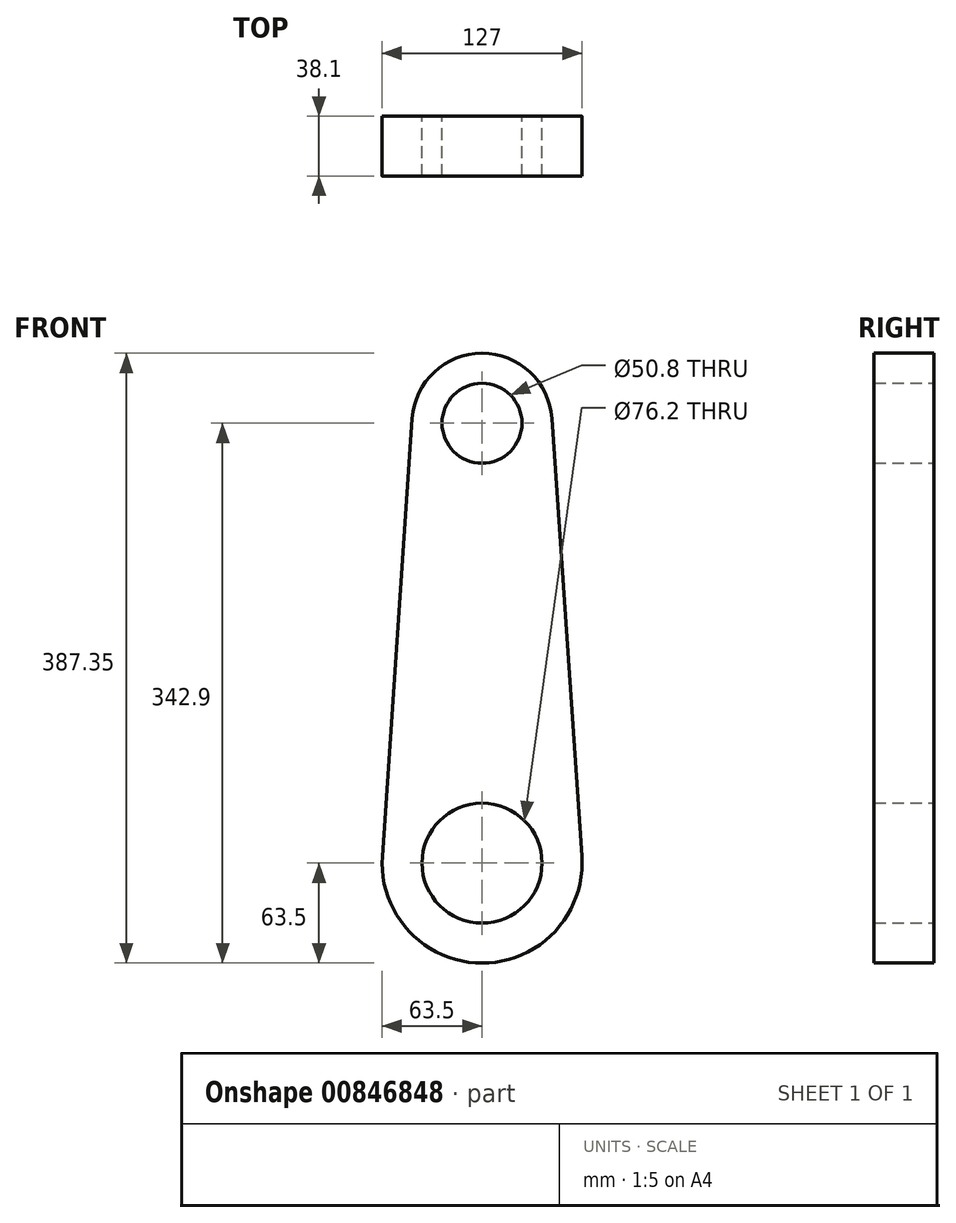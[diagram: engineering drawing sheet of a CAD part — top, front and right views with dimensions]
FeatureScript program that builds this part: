
annotation { "Feature Type Name" : "Feature", "Feature Type Description" : "" }
export const myFeature = defineFeature(function(context is Context, id is Id, definition is map)
    precondition{}
    {
        {
            var Q0;
            Q0=qCreatedBy(makeId("Front.planeOp"),FACE);
            var sketch = newSketch(context, id + "F0", { "sketchPlane" : qUnion([Q0])});
            skArc(sketch, "E0", {"start": v(-63.35, 4.33) * mm, "mid": v(0, -63.5) * mm, "end": v(63.35, 4.33) * mm});
            skArc(sketch, "E1", {"start": v(44.35, 282.43) * mm, "mid": v(0, 323.85) * mm, "end": v(-44.35, 282.43) * mm});
            skLineSegment(sketch, "E2", {"start": v(0, 0) * mm, "end": v(0, 279.4) * mm, "construction": true});
            skLineSegment(sketch, "E3", {"start": v(-44.35, 282.43) * mm, "end": v(-63.35, 4.33) * mm});
            skLineSegment(sketch, "E4", {"start": v(44.35, 282.43) * mm, "end": v(63.35, 4.33) * mm});
            skCircle(sketch, "E5", {"center": v(0, 279.4) * mm, "radius": 25.4 * mm});
            skCircle(sketch, "E6", {"center": v(0, 0) * mm, "radius": 38.1 * mm});
            skSolve(sketch);
        }
        {
            var Q0;
            Q0 = qSketchRegion(id + "F0", true);
            extrude(context, id + "F1", {"entities" : qUnion([Q0]), "depth" : 38.1 * mm, "offsetDistance" : 25.4 * mm, "symmetric" : true});
        }
    });
